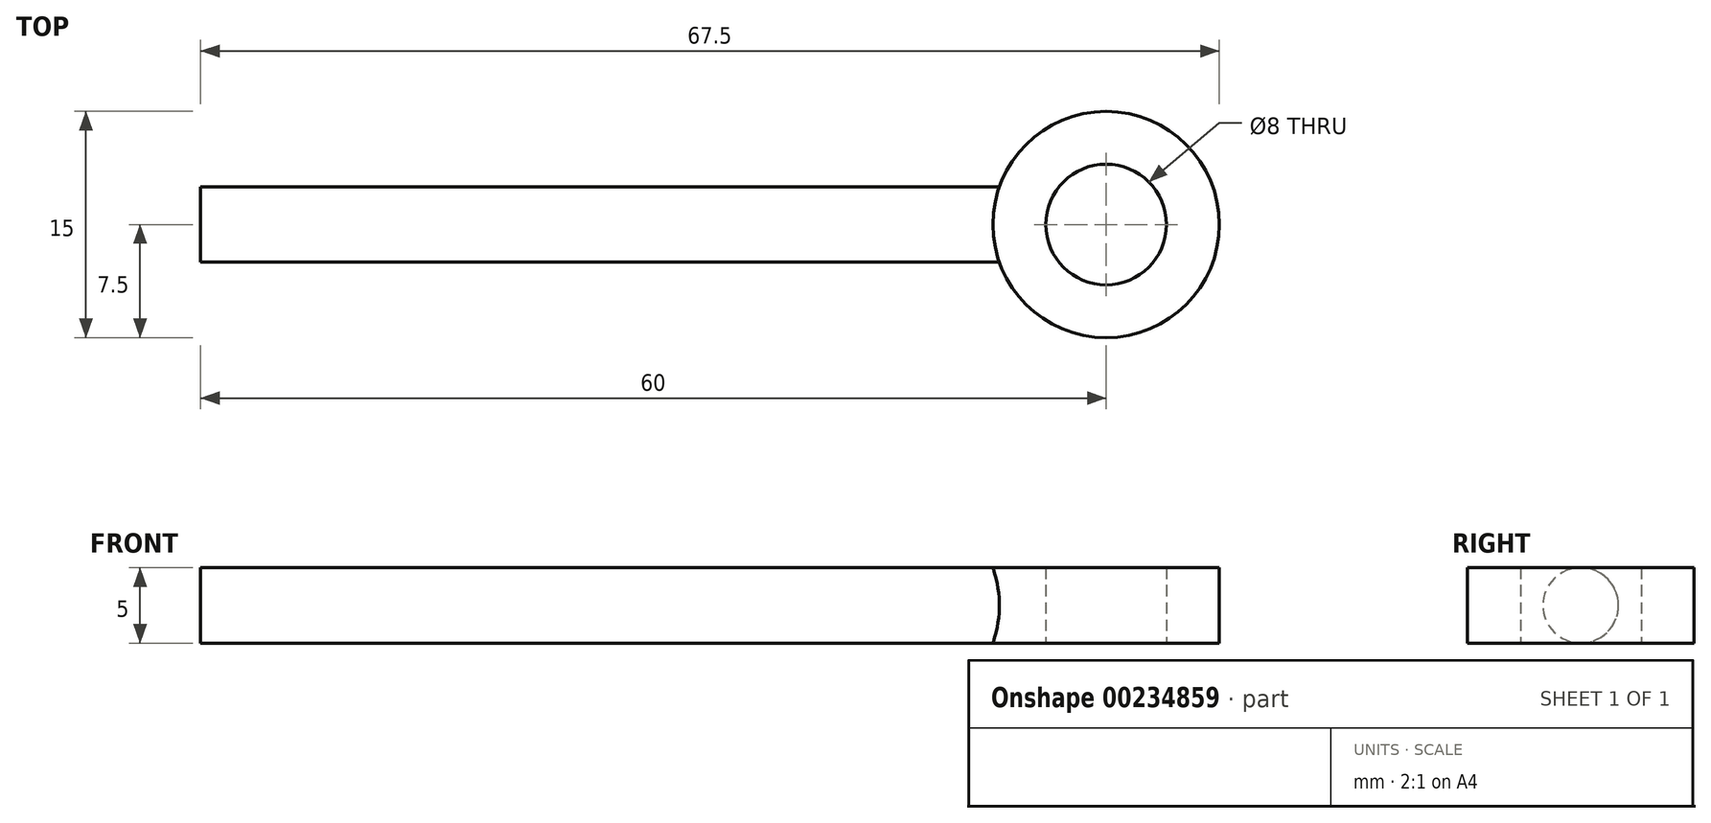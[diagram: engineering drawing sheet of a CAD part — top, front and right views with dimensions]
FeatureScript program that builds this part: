
annotation { "Feature Type Name" : "Feature", "Feature Type Description" : "" }
export const myFeature = defineFeature(function(context is Context, id is Id, definition is map)
    precondition{}
    {
        {
            var Q0;
            Q0=qCreatedBy(makeId("Top.planeOp"),FACE);
            var sketch = newSketch(context, id + "F0", { "sketchPlane" : qUnion([Q0])});
            skCircle(sketch, "E0", {"center": v(0, 0) * mm, "radius": 4 * mm});
            skCircle(sketch, "E1", {"center": v(0, 0) * mm, "radius": 7.5 * mm});
            skSolve(sketch);
        }
        {
            var Q0;
            Q0 = qSketchRegion(id + "F0", true);
            extrude(context, id + "F1", {"entities" : qUnion([Q0]), "depth" : 5 * mm, "symmetric" : true});
        }
        {
            var Q0;
            Q0=qCreatedBy(makeId("Right.planeOp"),FACE);
            cPlane(context, id + "F2", {"entities" : qUnion([Q0]), "cplaneType" : CPlaneType.OFFSET, "offset" : 60 * mm, "oppositeDirection" : true, "width" : 150 * mm, "height" : 150 * mm});
        }
        {
            var Q0;
            Q0=qCreatedBy(id+"F2.planeOp",FACE);
            var sketch = newSketch(context, id + "F3", { "sketchPlane" : qUnion([Q0])});
            skCircle(sketch, "E2", {"center": v(0, 0) * mm, "radius": 2.5 * mm});
            skSolve(sketch);
        }
        {
            var Q0;
            Q0 = qSketchRegion(id + "F3", true);
            extrude(context, id + "F4", {"entities" : qUnion([Q0]), "operationType" : NewBodyOperationType.ADD, "endBound" : BoundingType.UP_TO_NEXT, "depth" : 25 * mm});
        }
    });
